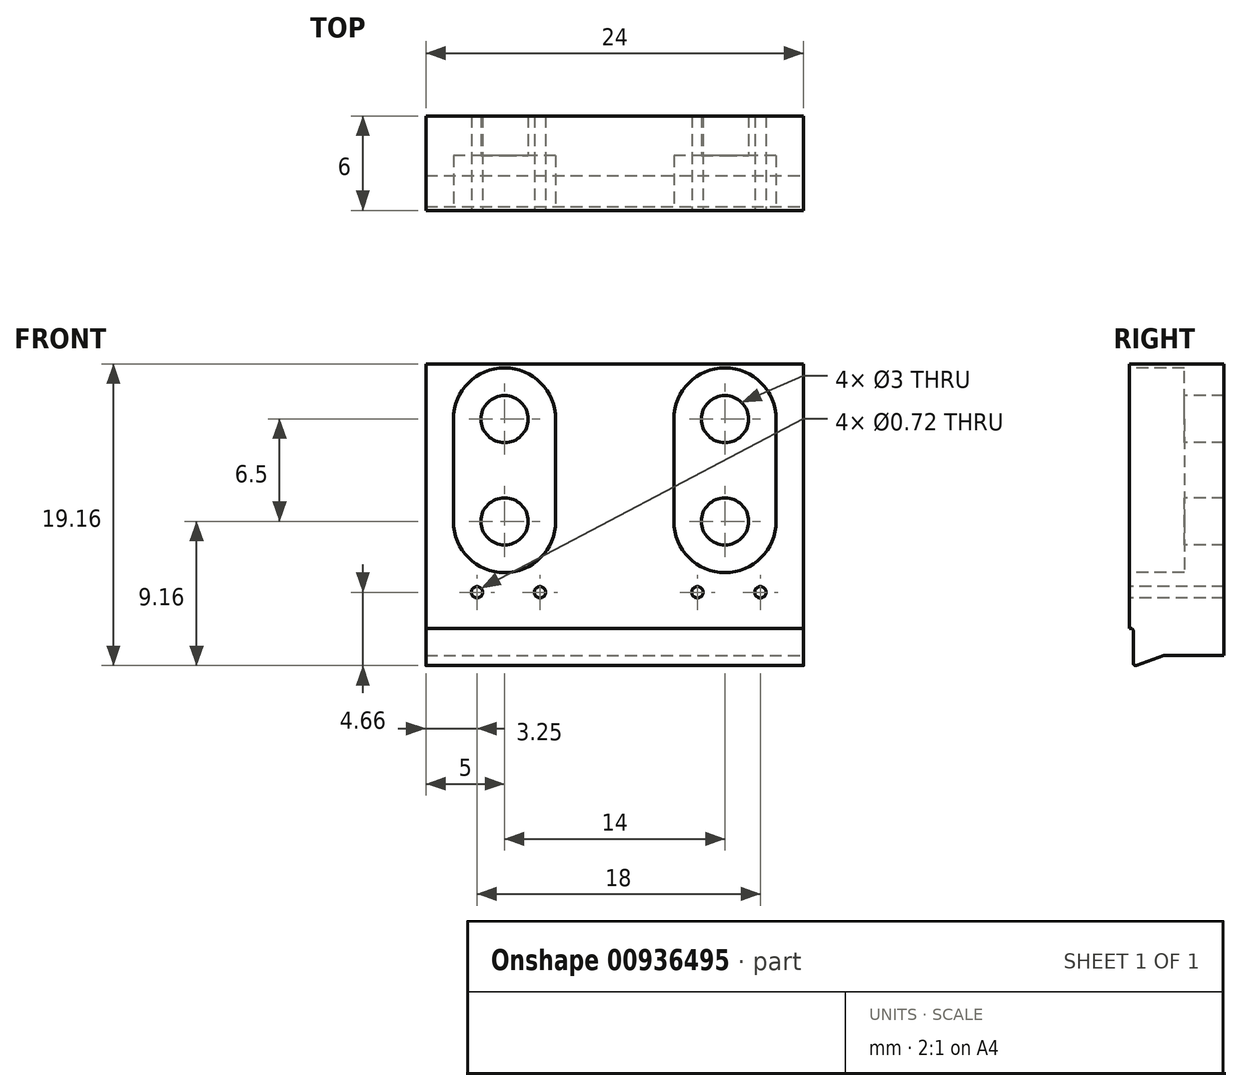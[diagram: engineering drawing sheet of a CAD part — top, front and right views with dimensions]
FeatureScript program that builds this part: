
annotation { "Feature Type Name" : "Feature", "Feature Type Description" : "" }
export const myFeature = defineFeature(function(context is Context, id is Id, definition is map)
    precondition{}
    {
        {
            var Q0;
            Q0=qCreatedBy(makeId("Front.planeOp"),FACE);
            var sketch = newSketch(context, id + "F0", { "sketchPlane" : qUnion([Q0])});
            skLineSegment(sketch, "E0.bottom", {"start": v(12, -9.6) * mm, "end": v(-12, -9.61) * mm});
            skLineSegment(sketch, "E0.top", {"start": v(12, 9.61) * mm, "end": v(-12, 9.6) * mm});
            skLineSegment(sketch, "E0.left", {"start": v(12, -9.6) * mm, "end": v(12, 9.61) * mm});
            skLineSegment(sketch, "E0.right", {"start": v(-12, -9.61) * mm, "end": v(-12, 9.6) * mm});
            skPoint(sketch, "E0.middle", {"position": v(0, 0) * mm});
            skSolve(sketch);
        }
        {
            var Q0;
            Q0 = qSketchRegion(id + "F0", true);
            extrude(context, id + "F1", {"entities" : qUnion([Q0]), "oppositeDirection" : true, "depth" : 6 * mm, "offsetDistance" : 25 * mm});
        }
        {
            var Q0;
            Q0=makeQuery(id+"F1.opExtrude","CAP_FACE",FACE,{"disambiguationData":[OSD([sQuery(id+"F0.wireOp",EDGE,"E0.bottom"),sQuery(id+"F0.wireOp",EDGE,"E0.top"),sQuery(id+"F0.wireOp",EDGE,"E0.left"),sQuery(id+"F0.wireOp",EDGE,"E0.right")])],"isStart":true});
            var sketch = newSketch(context, id + "F2", { "sketchPlane" : qUnion([Q0])});
            skLineSegment(sketch, "E1", {"start": v(-12, 9.6) * mm, "end": v(-7, 9.6) * mm});
            skLineSegment(sketch, "E2", {"start": v(-7, 9.6) * mm, "end": v(-7, -0.4) * mm});
            skLineSegment(sketch, "E3", {"start": v(-7, -0.4) * mm, "end": v(7, -0.4) * mm});
            skLineSegment(sketch, "E4", {"start": v(7, -0.4) * mm, "end": v(7, 9.61) * mm});
            skLineSegment(sketch, "E5", {"start": v(-7, 9.6) * mm, "end": v(-7, 6.11) * mm});
            skLineSegment(sketch, "E6", {"start": v(7, 9.61) * mm, "end": v(7, 6.11) * mm});
            skCircle(sketch, "E7", {"center": v(-7, 6.11) * mm, "radius": 1.5 * mm});
            skCircle(sketch, "E8", {"center": v(-7, -0.4) * mm, "radius": 1.5 * mm});
            skCircle(sketch, "E9", {"center": v(7, -0.4) * mm, "radius": 1.5 * mm});
            skCircle(sketch, "E10", {"center": v(7, 6.11) * mm, "radius": 1.5 * mm});
            skSolve(sketch);
        }
        {
            var Q0;
            Q0 = qSketchRegion(id + "F2", true);
            extrude(context, id + "F3", {"entities" : qUnion([Q0]), "operationType" : NewBodyOperationType.REMOVE, "endBound" : BoundingType.UP_TO_NEXT, "oppositeDirection" : true, "depth" : 25 * mm, "offsetDistance" : 25 * mm});
        }
        {
            var Q0;
            Q0=makeQuery(id+"F1.opExtrude","CAP_FACE",FACE,{"disambiguationData":[OSD([sQuery(id+"F0.wireOp",EDGE,"E0.bottom"),sQuery(id+"F0.wireOp",EDGE,"E0.top"),sQuery(id+"F0.wireOp",EDGE,"E0.left"),sQuery(id+"F0.wireOp",EDGE,"E0.right")])],"isStart":true});
            var sketch = newSketch(context, id + "F4", { "sketchPlane" : qUnion([Q0])});
            skArc(sketch, "E11", {"start": v(-10.25, 6.11) * mm, "mid": v(-7, 9.36) * mm, "end": v(-3.75, 6.11) * mm});
            skArc(sketch, "E12", {"start": v(-10.25, -0.4) * mm, "mid": v(-7, -3.64) * mm, "end": v(-3.75, -0.4) * mm});
            skArc(sketch, "E13", {"start": v(10.25, -0.4) * mm, "mid": v(7, -3.64) * mm, "end": v(3.75, -0.4) * mm});
            skArc(sketch, "E14", {"start": v(10.25, 6.11) * mm, "mid": v(7, 9.36) * mm, "end": v(3.75, 6.11) * mm});
            skLineSegment(sketch, "E15", {"start": v(-10.25, 6.11) * mm, "end": v(-10.25, -0.4) * mm});
            skLineSegment(sketch, "E16", {"start": v(-3.75, 6.11) * mm, "end": v(-3.75, -0.4) * mm});
            skLineSegment(sketch, "E17", {"start": v(10.25, 6.11) * mm, "end": v(10.25, -0.4) * mm});
            skLineSegment(sketch, "E18", {"start": v(3.75, -0.4) * mm, "end": v(3.75, 6.11) * mm});
            skSolve(sketch);
        }
        {
            var Q0;
            Q0 = qSketchRegion(id + "F4", true);
            extrude(context, id + "F5", {"entities" : qUnion([Q0]), "operationType" : NewBodyOperationType.REMOVE, "oppositeDirection" : true, "depth" : 3.5 * mm, "offsetDistance" : 25 * mm});
        }
        {
            var Q0;
            Q0=makeQuery(id+"F1.opExtrude","CAP_FACE",FACE,{"disambiguationData":[OSD([sQuery(id+"F0.wireOp",EDGE,"E0.bottom"),sQuery(id+"F0.wireOp",EDGE,"E0.top"),sQuery(id+"F0.wireOp",EDGE,"E0.left"),sQuery(id+"F0.wireOp",EDGE,"E0.right")])],"isStart":true});
            var sketch = newSketch(context, id + "F6", { "sketchPlane" : qUnion([Q0])});
            skLineSegment(sketch, "E19.bottom", {"start": v(-12, -9.61) * mm, "end": v(12, -9.61) * mm});
            skLineSegment(sketch, "E19.top", {"start": v(-12, -7.2) * mm, "end": v(12, -7.2) * mm});
            skLineSegment(sketch, "E19.left", {"start": v(-12, -9.61) * mm, "end": v(-12, -7.2) * mm});
            skLineSegment(sketch, "E19.right", {"start": v(12, -9.61) * mm, "end": v(12, -7.2) * mm});
            skSolve(sketch);
        }
        {
            var Q0;
            Q0 = qSketchRegion(id + "F6", true);
            extrude(context, id + "F7", {"entities" : qUnion([Q0]), "operationType" : NewBodyOperationType.REMOVE, "oppositeDirection" : true, "depth" : 0.25 * mm, "offsetDistance" : 25 * mm});
        }
        {
            var Q0;
            Q0=makeQuery(id+"F1.opExtrude","CAP_FACE",FACE,{"disambiguationData":[OSD([sQuery(id+"F0.wireOp",EDGE,"E0.bottom"),sQuery(id+"F0.wireOp",EDGE,"E0.top"),sQuery(id+"F0.wireOp",EDGE,"E0.left"),sQuery(id+"F0.wireOp",EDGE,"E0.right")])],"isStart":true});
            var sketch = newSketch(context, id + "F8", { "sketchPlane" : qUnion([Q0])});
            skLineSegment(sketch, "E20", {"start": v(-12, 9.6) * mm, "end": v(-8.75, 9.6) * mm});
            skLineSegment(sketch, "E21", {"start": v(-8.75, 9.61) * mm, "end": v(-8.75, -4.9) * mm});
            skLineSegment(sketch, "E22", {"start": v(-8.75, -4.9) * mm, "end": v(-4.75, -4.9) * mm});
            skLineSegment(sketch, "E23", {"start": v(-4.75, -4.9) * mm, "end": v(5.25, -4.89) * mm});
            skLineSegment(sketch, "E24", {"start": v(5.25, -4.89) * mm, "end": v(9.25, -4.9) * mm});
            skCircle(sketch, "E25", {"center": v(-8.75, -4.9) * mm, "radius": 0.36 * mm});
            skCircle(sketch, "E26", {"center": v(-4.75, -4.9) * mm, "radius": 0.36 * mm});
            skCircle(sketch, "E27", {"center": v(5.25, -4.89) * mm, "radius": 0.36 * mm});
            skCircle(sketch, "E28", {"center": v(9.25, -4.9) * mm, "radius": 0.36 * mm});
            skSolve(sketch);
        }
        {
            var Q0;
            Q0 = qSketchRegion(id + "F8", true);
            extrude(context, id + "F9", {"entities" : qUnion([Q0]), "operationType" : NewBodyOperationType.REMOVE, "endBound" : BoundingType.UP_TO_NEXT, "oppositeDirection" : true, "depth" : 25 * mm, "offsetDistance" : 25 * mm});
        }
        {
            var Q0;
            Q0=makeQuery(id+"F1.opExtrude","SWEPT_FACE",FACE,{"disambiguationData":[OSD([sQuery(id+"F0.wireOp",EDGE,"E0.left")])]});
            var sketch = newSketch(context, id + "F10", { "sketchPlane" : qUnion([Q0])});
            skLineSegment(sketch, "E29", {"start": v(0.25, -9.6) * mm, "end": v(2.2, -8.9) * mm});
            skLineSegment(sketch, "E30", {"start": v(2.2, -8.9) * mm, "end": v(6, -8.9) * mm});
            skLineSegment(sketch, "E31", {"start": v(6, -8.9) * mm, "end": v(6, -9.6) * mm});
            skLineSegment(sketch, "E32", {"start": v(6, -9.6) * mm, "end": v(0.25, -9.6) * mm});
            skSolve(sketch);
        }
        {
            var Q0;
            Q0 = qSketchRegion(id + "F10", true);
            extrude(context, id + "F11", {"entities" : qUnion([Q0]), "operationType" : NewBodyOperationType.REMOVE, "endBound" : BoundingType.UP_TO_NEXT, "oppositeDirection" : true, "depth" : 25 * mm, "offsetDistance" : 25 * mm});
        }
        {
            var Q0;
            {var subQ0=sQuery(id+"F6.wireOp",EDGE,"E19.bottom");Q0=makeQuery(id+"F11.boolean.opBoolean","MERGE",EDGE,{"derivedFrom":[makeQuery(id+"F7.boolean.opBoolean","COPY",EDGE,{"derivedFrom":makeQuery(id+"F7.opExtrude","CAP_EDGE",EDGE,{"disambiguationData":[OSD([subQ0])],"isStart":false})})],"fromTools":[makeQuery(id+"F11.opExtrude","SWEPT_EDGE",EDGE,{"disambiguationData":[OSD([subQ0,sQuery(id+"F6.wireOp",EDGE,"E19.left")])]})]});}
            fillet(context, id + "F12", {"entities" : qUnion([Q0]), "radius" : 0.15 * mm, "tangentPropagation" : true, "allowEdgeOverflow" : false});
        }
        {
            var Q0;
            Q0=makeQuery(id+"F7.boolean.opBoolean","COPY",EDGE,{"derivedFrom":makeQuery(id+"F7.opExtrude","CAP_EDGE",EDGE,{"disambiguationData":[OSD([sQuery(id+"F6.wireOp",EDGE,"E19.top")])],"isStart":false})});
            fillet(context, id + "F13", {"entities" : qUnion([Q0]), "radius" : 0.15 * mm, "tangentPropagation" : true, "allowEdgeOverflow" : false});
        }
    });
